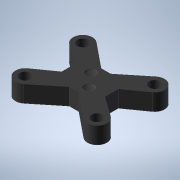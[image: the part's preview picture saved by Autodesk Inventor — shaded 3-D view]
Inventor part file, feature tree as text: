
AUTODESK INVENTOR PART (.ipt)
format: ipt  version: 2021 (Build 250183000, 183)  size: 991,232 bytes
history: native  units: mm
features: other x7, sketch x4, reference x2, extrude x1, mirror x1, plane x1, revolve x1, chamfer x1
ambient origin geometry x8: Origin, YZ Plane, XZ Plane, XY Plane, X Axis, Y Axis, Z Axis, Center Point
bodies: Volumenkörper1 (feature_tree)
feature tree (18):
  other  "Castor_Wheel.ipt"
  extrude  "Extrusion1"  Depth=10.0mm
  mirror  "Spiegeln1"
  sketch  "Skizze2"  dims[d3=4.0mm]
  plane  "Arbeitsebene1"
  sketch  "Skizze4"  dims[d4=10.0mm d5=4.0mm d6=2.0mm d7=2.0mm d8=7.0mm d9=0.0mm d10=60.0deg d11=3.8mm d12=0.6mm d13=3.1505mm d14=0.32475mm d15=0.06495mm d16=60.0deg d17=3.8mm d18=0.6mm d19=3.1505mm d20=0.5196mm d21=0.0mm d22=3.1505mm d23=90.0deg d24=0.6mm d25=7.0mm d26=10.0mm d27=0.0mm d28=90.0deg d29=90.0deg d30=0.0mm d31=0.0mm d32=0.5mm d33=2.0mm d34=45.0deg]
  revolve  "Umdrehung1"
  chamfer  "Fase1"  Distance=4.0mm
  other  "Spirale1"
  sketch  "Skizzenbasierte Anordnung1"  dims[d0=10.0mm d1=0.2mm]
  sketch  "Skizze1"  dims[d2=8.0mm]
  reference  "Referenz1"
  reference  "Referenz2"
  other  "Arbeitsachse1"
  other  "Arbeitsachse2"
  other  "<userpath>\Desktop\Bachelorarbeit\CAD\00_RobotAssembly.iam"
  other  "00_RobotAssembly.iam"
  other  "08_HolderSR04:1"
